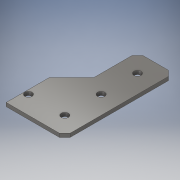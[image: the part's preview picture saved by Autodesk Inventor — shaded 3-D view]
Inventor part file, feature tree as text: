
AUTODESK INVENTOR PART (.ipt)
format: ipt  version: 2017 (Build 210142000, 142)  size: 115,200 bytes
history: native  units: in
note: dims shown in document units (in); Inventor stores cm internally (conversion verified against a paired STEP export)
features: extrude x2, sketch x2
ambient origin geometry x8: Origin, YZ Plane, XZ Plane, XY Plane, X Axis, Y Axis, Z Axis, Center Point
bodies: Body1 (feature_tree)
feature tree (4):
  extrude  "Extrusion2"  Depth=0.1in TaperAngle=0.0deg
  extrude  "Extrusion3"  [1 undecoded]
  sketch  "Sketch1"  dims[d26=0.1in d27=0.0in d28=0.1875in d29=0.0in]
  sketch  "Sketch2"
note: 1 required parameter value undecoded (feature->parameter linkage not recoverable at this tier; creation-order binding heuristic only, values carry confidence <= 0.55)
